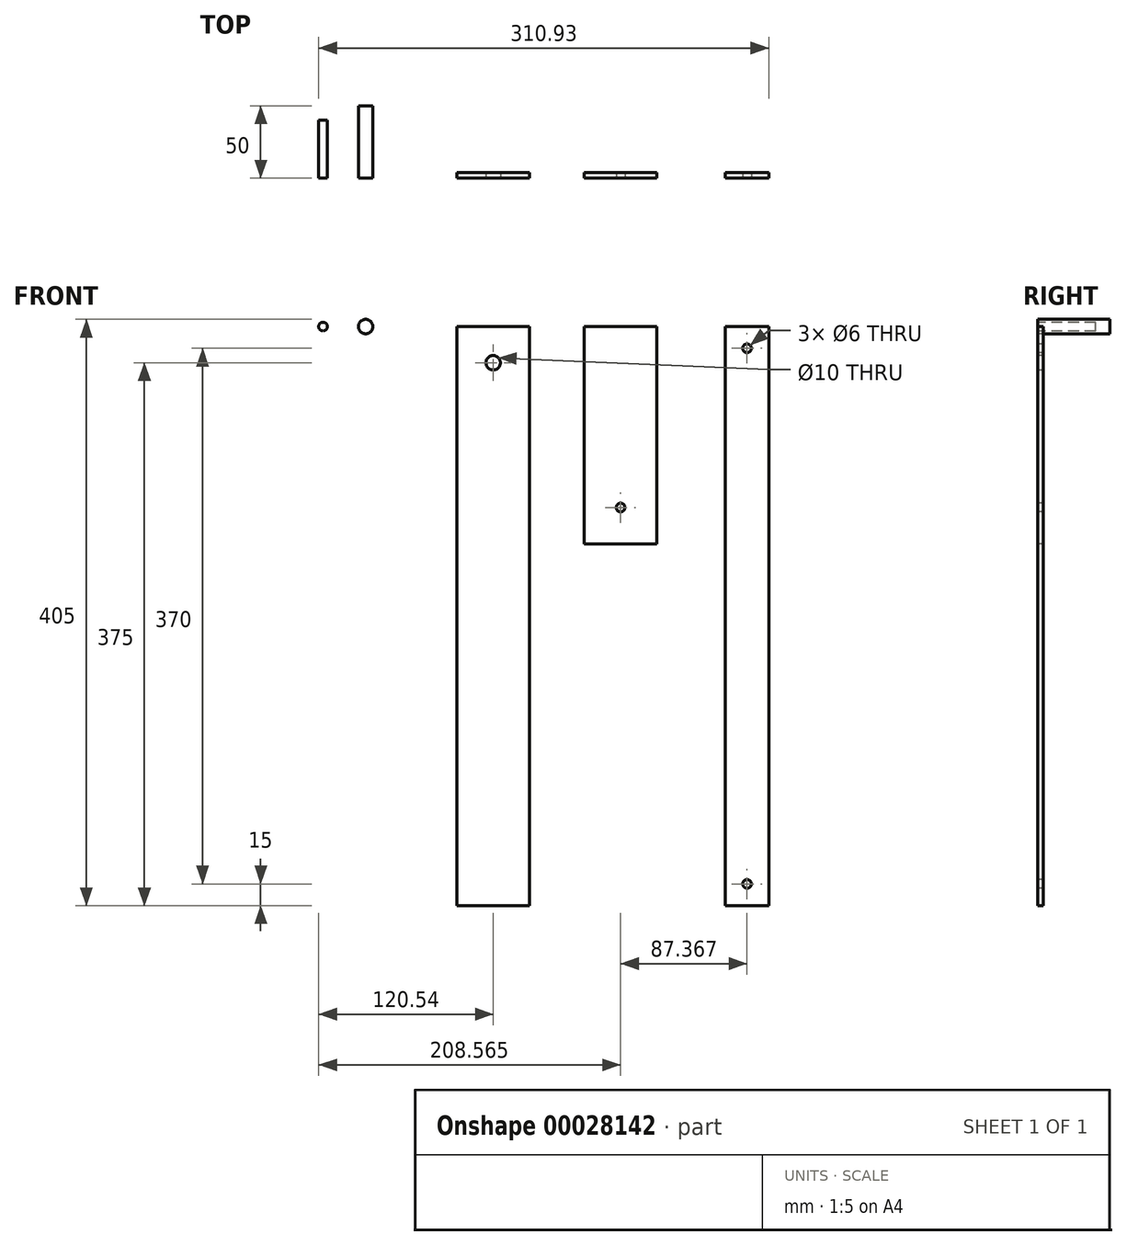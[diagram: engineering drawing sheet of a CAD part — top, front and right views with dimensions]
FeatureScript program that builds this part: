
annotation { "Feature Type Name" : "Feature", "Feature Type Description" : "" }
export const myFeature = defineFeature(function(context is Context, id is Id, definition is map)
    precondition{}
    {
        {
            var Q0;
            Q0=qCreatedBy(makeId("Front.planeOp"),FACE);
            var sketch = newSketch(context, id + "F0", { "sketchPlane" : qUnion([Q0])});
            skLineSegment(sketch, "E0.bottom", {"start": v(0, 0) * mm, "end": v(-50, 0) * mm});
            skLineSegment(sketch, "E0.top", {"start": v(0, -400) * mm, "end": v(-50, -400) * mm});
            skLineSegment(sketch, "E0.left", {"start": v(0, 0) * mm, "end": v(0, -400) * mm});
            skLineSegment(sketch, "E0.right", {"start": v(-50, 0) * mm, "end": v(-50, -400) * mm});
            skSolve(sketch);
        }
        {
            var Q0;
            Q0=makeQuery(id+"F0.imprint","IMPRINT",FACE,{"disambiguationData":[TD([[makeQuery(id+"F0.imprint","IMPRINT",EDGE,{"derivedFrom":sQuery(id+"F0.wireOp",EDGE,"E0.bottom")}),1.0]])]});
            extrude(context, id + "F1", {"entities" : qUnion([Q0]), "oppositeDirection" : true, "depth" : 4 * mm});
        }
        {
            var Q0;
            Q0=qCreatedBy(makeId("Front.planeOp"),FACE);
            var sketch = newSketch(context, id + "F2", { "sketchPlane" : qUnion([Q0])});
            skLineSegment(sketch, "E1.bottom", {"start": v(38.03, 0) * mm, "end": v(88.03, 0) * mm});
            skLineSegment(sketch, "E1.top", {"start": v(38.03, -150) * mm, "end": v(88.03, -150) * mm});
            skLineSegment(sketch, "E1.left", {"start": v(38.03, 0) * mm, "end": v(38.03, -150) * mm});
            skLineSegment(sketch, "E1.right", {"start": v(88.03, 0) * mm, "end": v(88.03, -150) * mm});
            skSolve(sketch);
        }
        {
            var Q0;
            Q0=makeQuery(id+"F2.imprint","IMPRINT",FACE,{"disambiguationData":[TD([[makeQuery(id+"F2.imprint","IMPRINT",EDGE,{"derivedFrom":sQuery(id+"F2.wireOp",EDGE,"E1.bottom")}),-1.0]])]});
            extrude(context, id + "F3", {"entities" : qUnion([Q0]), "oppositeDirection" : true, "depth" : 4 * mm});
        }
        {
            var Q0;
            Q0=qCreatedBy(makeId("Front.planeOp"),FACE);
            var sketch = newSketch(context, id + "F4", { "sketchPlane" : qUnion([Q0])});
            skCircle(sketch, "E2", {"center": v(-113.11, 0) * mm, "radius": 5 * mm});
            skSolve(sketch);
        }
        {
            var Q0;
            Q0=makeQuery(id+"F4.imprint","IMPRINT",FACE,{"disambiguationData":[TD([[makeQuery(id+"F4.imprint","IMPRINT",EDGE,{"derivedFrom":sQuery(id+"F4.wireOp",EDGE,"E2")}),1.0]])]});
            extrude(context, id + "F5", {"entities" : qUnion([Q0]), "oppositeDirection" : true, "depth" : 50 * mm});
        }
        {
            var Q0;
            Q0=makeQuery(id+"F1.opExtrude","CAP_FACE",FACE,{"disambiguationData":[OSD([sQuery(id+"F0.wireOp",EDGE,"E0.bottom"),sQuery(id+"F0.wireOp",EDGE,"E0.top"),sQuery(id+"F0.wireOp",EDGE,"E0.left"),sQuery(id+"F0.wireOp",EDGE,"E0.right")])],"isStart":true});
            var sketch = newSketch(context, id + "F6", { "sketchPlane" : qUnion([Q0])});
            skCircle(sketch, "E3", {"center": v(-25, -25) * mm, "radius": 5 * mm});
            skSolve(sketch);
        }
        {
            var Q0;
            Q0=makeQuery(id+"F6.imprint","IMPRINT",FACE,{"disambiguationData":[TD([[makeQuery(id+"F6.imprint","IMPRINT",EDGE,{"derivedFrom":sQuery(id+"F6.wireOp",EDGE,"E3")}),1.0]])]});
            extrude(context, id + "F7", {"entities" : qUnion([Q0]), "operationType" : NewBodyOperationType.REMOVE, "endBound" : BoundingType.UP_TO_NEXT, "oppositeDirection" : true, "depth" : 25 * mm});
        }
        {
            var Q0;
            Q0=makeQuery(id+"F3.opExtrude","CAP_FACE",FACE,{"disambiguationData":[OSD([sQuery(id+"F2.wireOp",EDGE,"E1.bottom"),sQuery(id+"F2.wireOp",EDGE,"E1.top"),sQuery(id+"F2.wireOp",EDGE,"E1.left"),sQuery(id+"F2.wireOp",EDGE,"E1.right")])],"isStart":true});
            var sketch = newSketch(context, id + "F8", { "sketchPlane" : qUnion([Q0])});
            skPoint(sketch, "E4", {"position": v(63.03, -125) * mm});
            skSolve(sketch);
        }
        {
            var Q0;
            Q0=sQuery(id+"F8.wireOp",VERTEX,"E4");
            var Q1;
            Q1=makeQuery(id+"F3.opExtrude","SWEPT_BODY",BODY,{"disambiguationData":[OSD([sQuery(id+"F2.wireOp",EDGE,"E1.bottom"),sQuery(id+"F2.wireOp",EDGE,"E1.top"),sQuery(id+"F2.wireOp",EDGE,"E1.left"),sQuery(id+"F2.wireOp",EDGE,"E1.right")])]});
            hole(context, id + "F9", {"style" : HoleStyle.SIMPLE, "holeDiameter" : 6 * mm, "endStyle" : HoleEndStyle.THROUGH, "locations" : qUnion([Q0]), "scope" : qUnion([Q1])});
        }
        {
            var Q0;
            Q0=qCreatedBy(makeId("Front.planeOp"),FACE);
            var sketch = newSketch(context, id + "F10", { "sketchPlane" : qUnion([Q0])});
            skLineSegment(sketch, "E5.bottom", {"start": v(135.4, 0) * mm, "end": v(165.4, 0) * mm});
            skLineSegment(sketch, "E5.top", {"start": v(135.4, -400) * mm, "end": v(165.4, -400) * mm});
            skLineSegment(sketch, "E5.left", {"start": v(135.4, 0) * mm, "end": v(135.4, -400) * mm});
            skLineSegment(sketch, "E5.right", {"start": v(165.4, 0) * mm, "end": v(165.4, -400) * mm});
            skSolve(sketch);
        }
        {
            var Q0;
            Q0=makeQuery(id+"F10.imprint","IMPRINT",FACE,{"disambiguationData":[TD([[makeQuery(id+"F10.imprint","IMPRINT",EDGE,{"derivedFrom":sQuery(id+"F10.wireOp",EDGE,"E5.bottom")}),-1.0]])]});
            extrude(context, id + "F11", {"entities" : qUnion([Q0]), "oppositeDirection" : true, "depth" : 4 * mm});
        }
        {
            var Q0;
            Q0=makeQuery(id+"F11.opExtrude","CAP_FACE",FACE,{"disambiguationData":[OSD([sQuery(id+"F10.wireOp",EDGE,"E5.bottom"),sQuery(id+"F10.wireOp",EDGE,"E5.top"),sQuery(id+"F10.wireOp",EDGE,"E5.left"),sQuery(id+"F10.wireOp",EDGE,"E5.right")])],"isStart":true});
            var sketch = newSketch(context, id + "F12", { "sketchPlane" : qUnion([Q0])});
            skPoint(sketch, "E6", {"position": v(150.4, -385) * mm});
            skPoint(sketch, "E7", {"position": v(150.4, -15) * mm});
            skSolve(sketch);
        }
        {
            var Q0;
            Q0=sQuery(id+"F12.wireOp",VERTEX,"E6");
            var Q1;
            Q1=sQuery(id+"F12.wireOp",VERTEX,"E7");
            var Q2;
            Q2=makeQuery(id+"F11.opExtrude","SWEPT_BODY",BODY,{"disambiguationData":[OSD([sQuery(id+"F10.wireOp",EDGE,"E5.bottom"),sQuery(id+"F10.wireOp",EDGE,"E5.top"),sQuery(id+"F10.wireOp",EDGE,"E5.left"),sQuery(id+"F10.wireOp",EDGE,"E5.right")])]});
            hole(context, id + "F13", {"style" : HoleStyle.SIMPLE, "holeDiameter" : 6 * mm, "endStyle" : HoleEndStyle.THROUGH, "locations" : qUnion([Q0, Q1]), "scope" : qUnion([Q2])});
        }
        {
            var Q0;
            Q0=qCreatedBy(makeId("Front.planeOp"),FACE);
            var sketch = newSketch(context, id + "F14", { "sketchPlane" : qUnion([Q0])});
            skCircle(sketch, "E8", {"center": v(-142.54, 0) * mm, "radius": 3 * mm});
            skSolve(sketch);
        }
        {
            var Q0;
            Q0=makeQuery(id+"F14.imprint","IMPRINT",FACE,{"disambiguationData":[TD([[makeQuery(id+"F14.imprint","IMPRINT",EDGE,{"derivedFrom":sQuery(id+"F14.wireOp",EDGE,"E8")}),1.0]])]});
            extrude(context, id + "F15", {"entities" : qUnion([Q0]), "oppositeDirection" : true, "depth" : 40 * mm});
        }
    });
